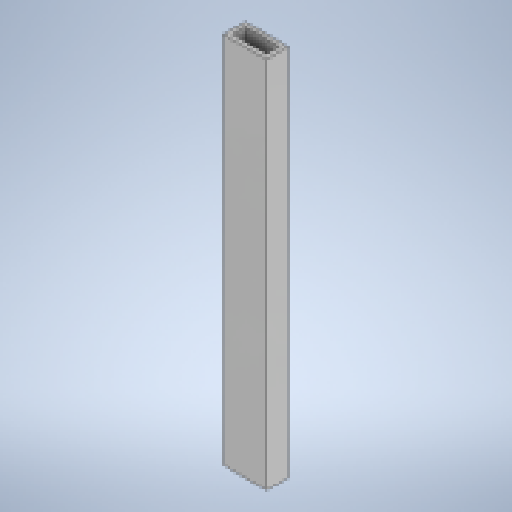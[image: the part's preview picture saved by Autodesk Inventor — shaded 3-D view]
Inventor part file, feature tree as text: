
AUTODESK INVENTOR PART (.ipt)
format: ipt  version: 2023 (Build 270158000, 158)  size: 154,112 bytes
history: native  units: mm
features: extrude x2, sketch x1
ambient origin geometry x8: Origin, YZ Plane, XZ Plane, XY Plane, X Axis, Y Axis, Z Axis, Center Point
bodies: Solid1 (feature_tree)
feature tree (3):
  sketch  "Sketch1"  dims[d0=20.3mm d1=10.3mm d2=2.2mm d3=150.0mm d4=0.0mm d5=25.0mm d6=0.0mm]
  extrude  "Extrusion1"  Depth=10.3mm
  extrude  "Extrusion2"  Depth=2.2mm
